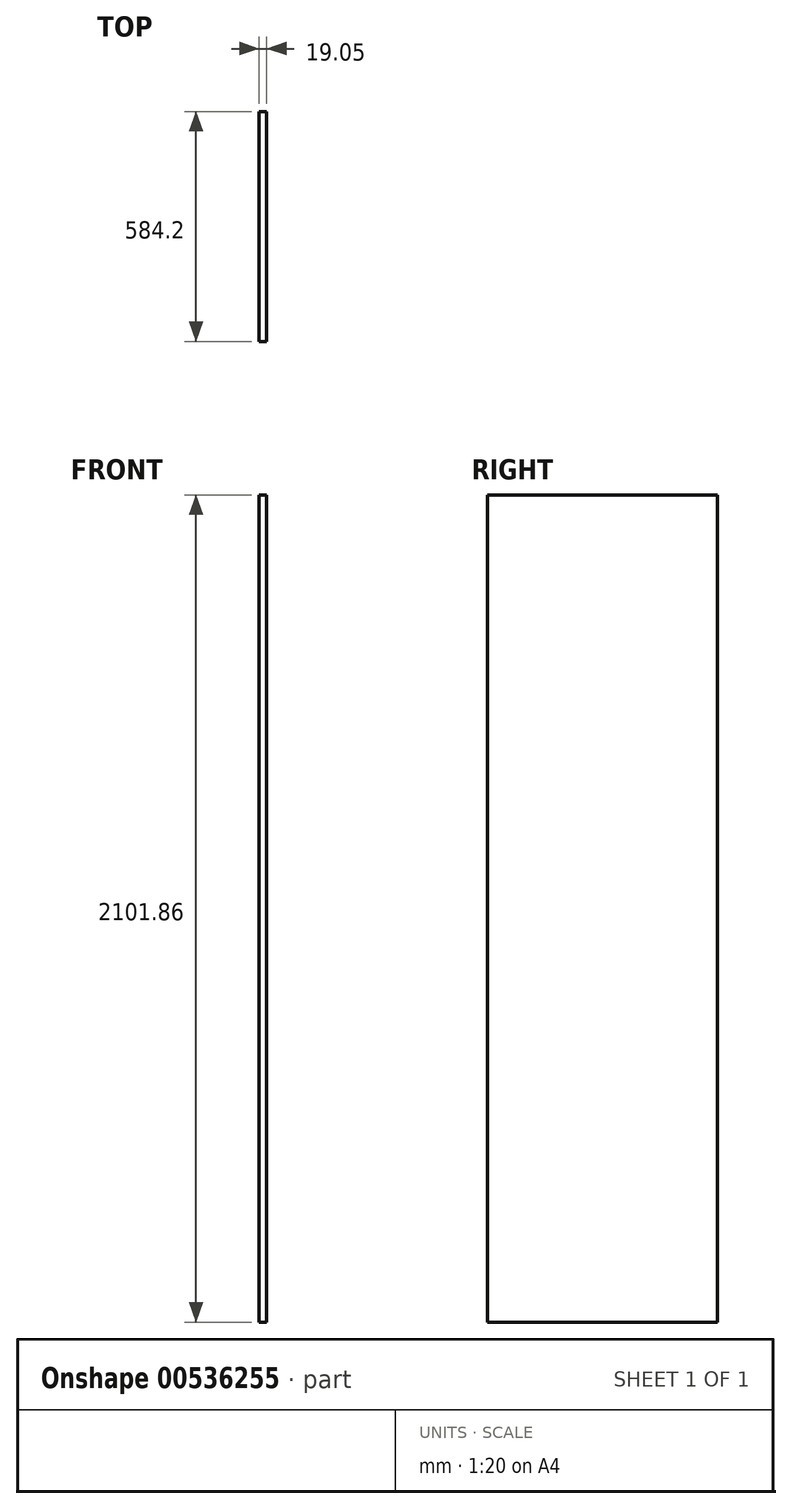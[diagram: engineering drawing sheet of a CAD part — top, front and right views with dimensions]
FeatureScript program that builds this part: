
annotation { "Feature Type Name" : "Feature", "Feature Type Description" : "" }
export const myFeature = defineFeature(function(context is Context, id is Id, definition is map)
    precondition{}
    {
        {
            var Q0;
            Q0=qCreatedBy(makeId("Right.planeOp"),FACE);
            var sketch = newSketch(context, id + "F0", { "sketchPlane" : qUnion([Q0])});
            skLineSegment(sketch, "E0.bottom", {"start": v(292.1, 1050.93) * mm, "end": v(-292.1, 1050.93) * mm});
            skLineSegment(sketch, "E0.top", {"start": v(292.1, -1050.93) * mm, "end": v(-292.1, -1050.93) * mm});
            skLineSegment(sketch, "E0.left", {"start": v(292.1, 1050.93) * mm, "end": v(292.1, -1050.93) * mm});
            skLineSegment(sketch, "E0.right", {"start": v(-292.1, 1050.93) * mm, "end": v(-292.1, -1050.93) * mm});
            skPoint(sketch, "E0.middle", {"position": v(0, 0) * mm});
            skSolve(sketch);
        }
        {
            var Q0;
            Q0 = qSketchRegion(id + "F0", true);
            extrude(context, id + "F1", {"entities" : qUnion([Q0]), "depth" : 28.57 * mm, "offsetDistance" : 25.4 * mm});
        }
        {
            var Q0;
            Q0=makeQuery(id+"F1.opExtrude","CAP_FACE",FACE,{"disambiguationData":[OSD([sQuery(id+"F0.wireOp",EDGE,"E0.bottom"),sQuery(id+"F0.wireOp",EDGE,"E0.top"),sQuery(id+"F0.wireOp",EDGE,"E0.left"),sQuery(id+"F0.wireOp",EDGE,"E0.right")])],"isStart":false});
            extrude(context, id + "F2", {"entities" : qUnion([Q0]), "operationType" : NewBodyOperationType.REMOVE, "oppositeDirection" : true, "depth" : 9.52 * mm, "offsetDistance" : 25.4 * mm});
        }
    });
